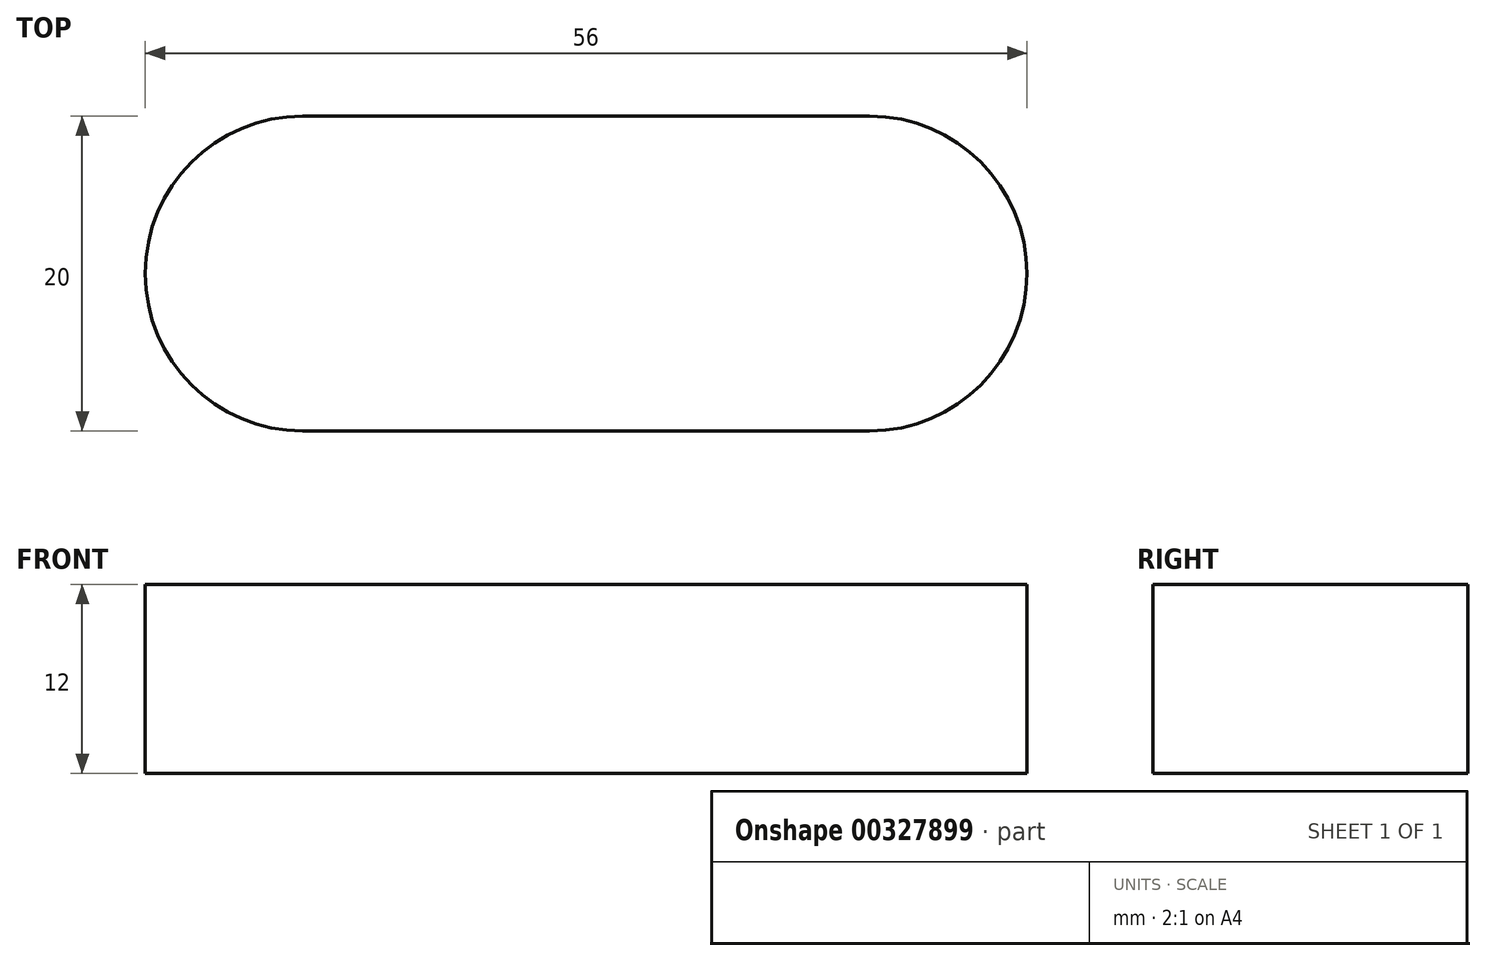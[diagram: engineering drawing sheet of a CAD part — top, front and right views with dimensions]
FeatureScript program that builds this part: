
annotation { "Feature Type Name" : "Feature", "Feature Type Description" : "" }
export const myFeature = defineFeature(function(context is Context, id is Id, definition is map)
    precondition{}
    {
        {
            var Q0;
            Q0=qCreatedBy(makeId("Top.planeOp"),FACE);
            var sketch = newSketch(context, id + "F0", { "sketchPlane" : qUnion([Q0])});
            skLineSegment(sketch, "E0.bottom", {"start": v(18, 10) * mm, "end": v(-18, 10) * mm});
            skLineSegment(sketch, "E0.top", {"start": v(18, -10) * mm, "end": v(-18, -10) * mm});
            skLineSegment(sketch, "E0.left", {"start": v(28, 0) * mm, "end": v(28, 0) * mm});
            skLineSegment(sketch, "E0.right", {"start": v(-28, 0) * mm, "end": v(-28, 0) * mm});
            skPoint(sketch, "E0.middle", {"position": v(0, 0) * mm});
            skPoint(sketch, "E1.visualSharp", {"position": v(-28, 10) * mm});
            skArc(sketch, "E1.filletArc", {"start": v(-18, 10) * mm, "mid": v(-25.07, 7.07) * mm, "end": v(-28, 0) * mm});
            skPoint(sketch, "E2.visualSharp", {"position": v(-28, -10) * mm});
            skArc(sketch, "E2.filletArc", {"start": v(-28, 0) * mm, "mid": v(-25.07, -7.07) * mm, "end": v(-18, -10) * mm});
            skPoint(sketch, "E3.visualSharp", {"position": v(28, -10) * mm});
            skArc(sketch, "E3.filletArc", {"start": v(18, -10) * mm, "mid": v(25.07, -7.07) * mm, "end": v(28, 0) * mm});
            skPoint(sketch, "E4.visualSharp", {"position": v(28, 10) * mm});
            skArc(sketch, "E4.filletArc", {"start": v(28, 0) * mm, "mid": v(25.07, 7.07) * mm, "end": v(18, 10) * mm});
            skSolve(sketch);
        }
        {
            var Q0;
            Q0=makeQuery(id+"F0.imprint","IMPRINT",FACE,{"disambiguationData":[TD([[makeQuery(id+"F0.imprint","IMPRINT",EDGE,{"derivedFrom":sQuery(id+"F0.wireOp",EDGE,"E0.bottom")}),1.0]])]});
            extrude(context, id + "F1", {"entities" : qUnion([Q0]), "depth" : 12 * mm});
        }
    });
